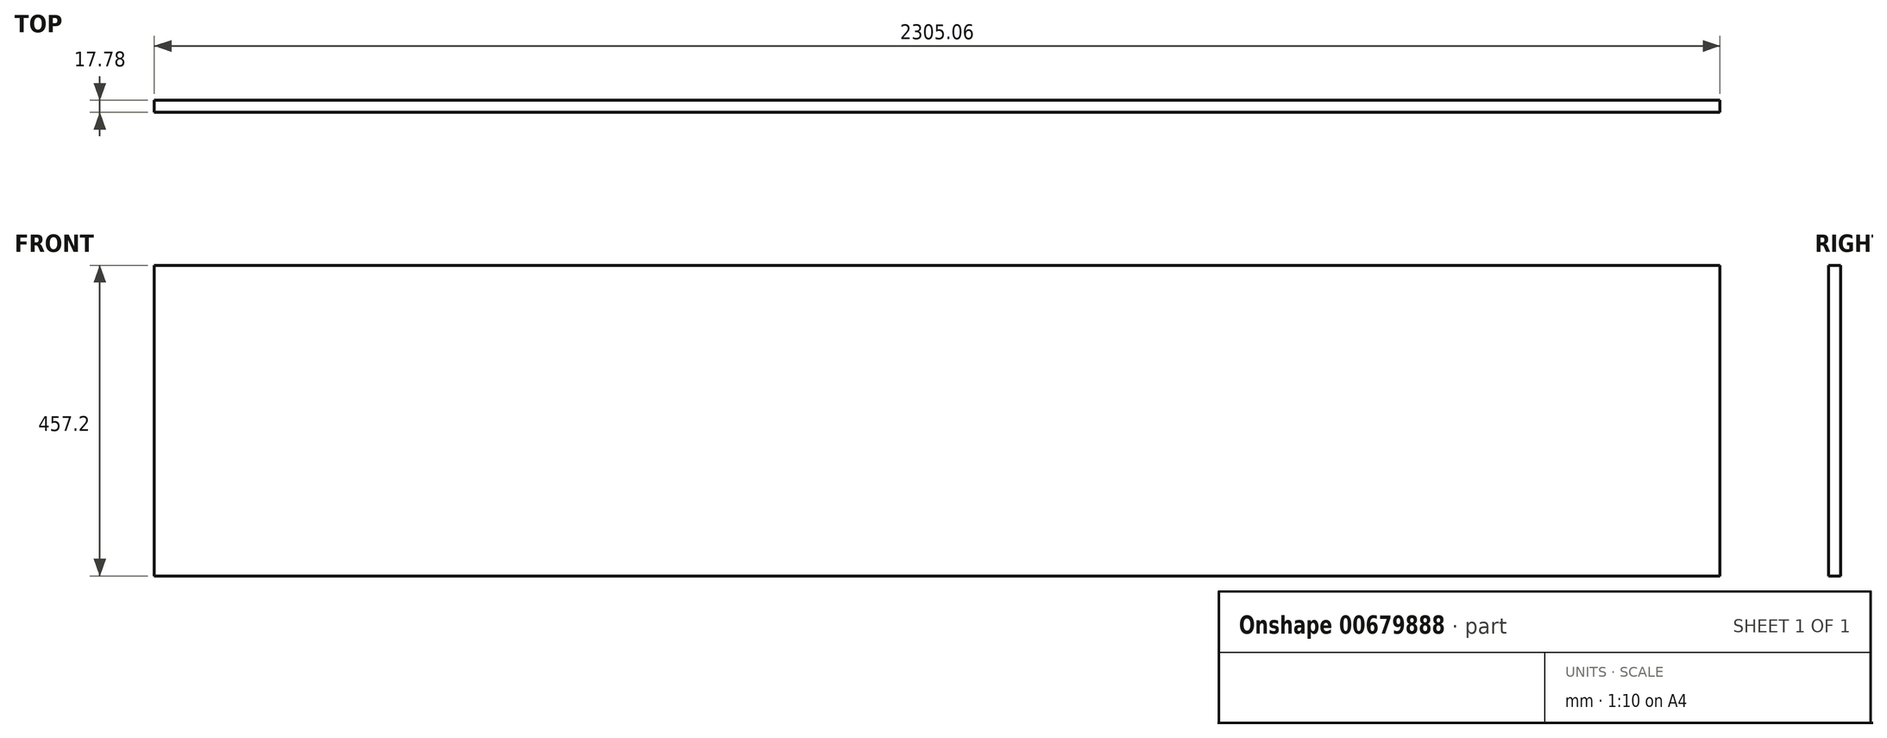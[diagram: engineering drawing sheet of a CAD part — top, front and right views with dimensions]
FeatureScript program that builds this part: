
annotation { "Feature Type Name" : "Feature", "Feature Type Description" : "" }
export const myFeature = defineFeature(function(context is Context, id is Id, definition is map)
    precondition{}
    {
        {
            var Q0;
            Q0=qCreatedBy(makeId("Front.planeOp"),FACE);
            var sketch = newSketch(context, id + "F0", { "sketchPlane" : qUnion([Q0])});
            skLineSegment(sketch, "E0.bottom", {"start": v(1152.53, 228.6) * mm, "end": v(-1152.53, 228.6) * mm});
            skLineSegment(sketch, "E0.top", {"start": v(1152.53, -228.6) * mm, "end": v(-1152.53, -228.6) * mm});
            skLineSegment(sketch, "E0.left", {"start": v(1152.53, 228.6) * mm, "end": v(1152.53, -228.6) * mm});
            skLineSegment(sketch, "E0.right", {"start": v(-1152.53, 228.6) * mm, "end": v(-1152.53, -228.6) * mm});
            skPoint(sketch, "E0.middle", {"position": v(0, 0) * mm});
            skSolve(sketch);
        }
        {
            var Q0;
            Q0=makeQuery(id+"F0.imprint","IMPRINT",FACE,{"disambiguationData":[TD([[makeQuery(id+"F0.imprint","IMPRINT",EDGE,{"derivedFrom":sQuery(id+"F0.wireOp",EDGE,"E0.bottom")}),1.0]])]});
            extrude(context, id + "F1", {"entities" : qUnion([Q0]), "endBound" : BoundingType.SYMMETRIC, "depth" : 17.78 * mm, "offsetDistance" : 25.4 * mm});
        }
    });
